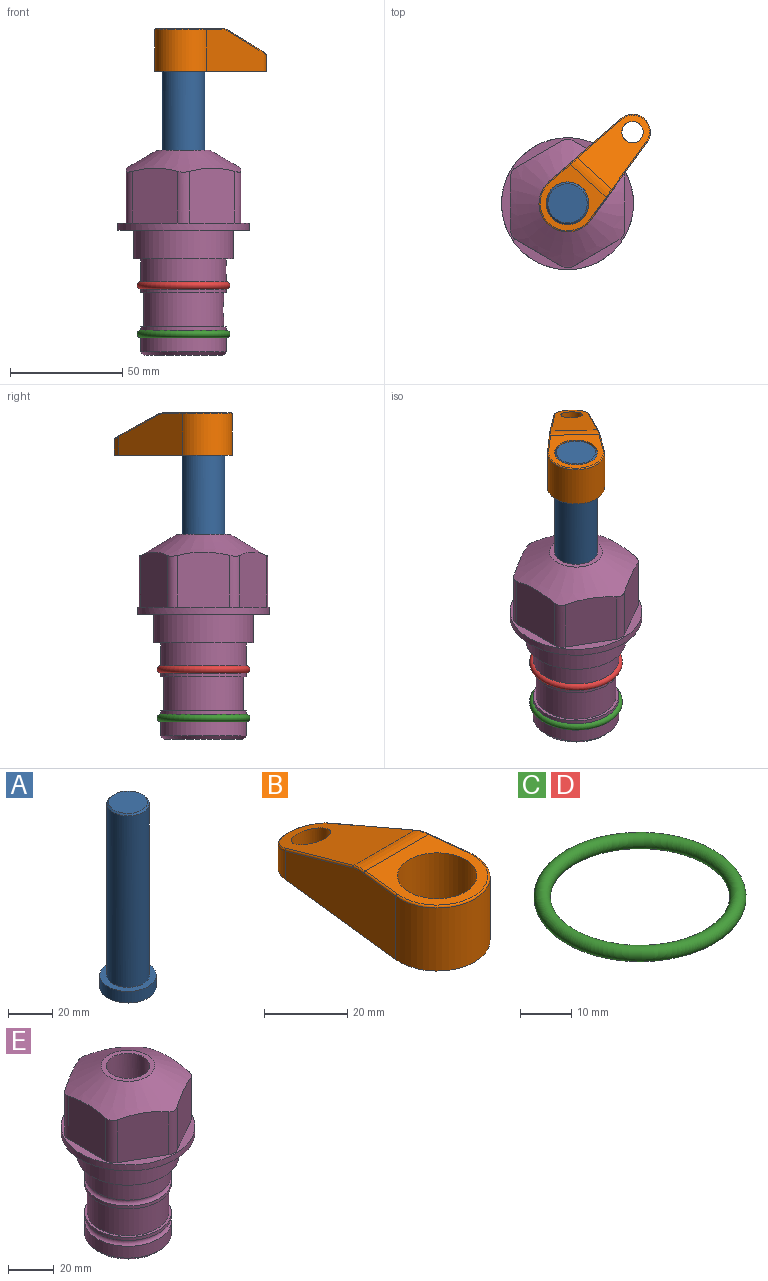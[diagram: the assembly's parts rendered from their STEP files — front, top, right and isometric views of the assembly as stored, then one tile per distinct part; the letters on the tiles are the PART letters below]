
ASSEMBLY  parts=5 mates=3
PART A: 6 faces, bbox 25.4x25.4x101.6 mm
  f0: plane 17.46x17.46mm, normal (0,0,1), area 239.5mm2, adj f5
  f1: plane 25.4x25.4mm, normal (0,0,-1), area 506.7mm2, adj f2
  f2: cylinder r=12.7mm len=25.4mm, axis (0,0,1), area 506.7mm2, adj f1,f3
  f3: plane 25.4x25.4mm, normal (0,0,1), area 221.7mm2, adj f2,f4
  f4: cylinder r=9.53mm len=94.46mm, axis (0,0,1), area 5653mm2, adj f3,f5
  f5: cone r=8.73mm half-angle=45deg, axis (0,0,-1), area 64.4mm2, adj f0,f4
PART B: 44 faces, bbox 27.5x64.5x19.1 mm
  f0: plane 2.3x0.95mm, normal (0,0,-1), area 1mm2, adj f25,f30,f34
  f1: plane 63.5x25.4mm, normal (0,0,-1), area 561.7mm2, adj f2,f3,f4,f5,f6,f7,f19,f20
  f2: cylinder r=12.7mm len=25.4mm, axis (0,0,-1), area 792.2mm2, adj f1,f3,f5,f13
  f3: plane 42.33x18.54mm, normal (0.99,0.11,0), area 647mm2, adj f1,f2,f4,f11,f12,f14
  f4: cylinder r=7.94mm len=15.78mm, axis (0,0,-1), area 158.6mm2, adj f1,f3,f5,f16
  f5: plane 42.33x18.54mm, normal (-0.99,0.11,0), area 647mm2, adj f1,f2,f4,f15,f17,f18
  f6: cylinder r=9.53mm len=19.05mm, axis (0,0,-1), area 1140.1mm2, adj f1,f8
  f7: cylinder r=4.76mm len=10.98mm, axis (0,0,-1), area 276.1mm2, adj f1,f9
  f8: plane 25.83x24.38mm, normal (0,0,1), area 262.2mm2, adj f6,f10,f11,f13,f15
  f9: plane 32.49x20.55mm, normal (0,0.34,0.94), area 489.9mm2, adj f7,f10,f14,f16,f18
  f10: cylinder r=12.7mm len=21.49mm, axis (-1,0,0), area 93.2mm2, adj f8,f9,f12,f17
  f11: cylinder r=0.51mm len=12.34mm, axis (0.11,-0.99,0), area 9.9mm2, adj f3,f8,f12,f13
  f12: bspline ~7.62x1.64mm, area 3.5mm2, adj f3,f10,f11,f14
  f13: torus R=12.19mm, axis (0,0,1), area 33.6mm2, adj f2,f8,f11,f15
  f14: cylinder r=0.51mm len=26.01mm, axis (0.1,-0.93,0.34), area 21.6mm2, adj f3,f9,f12,f16
  f15: cylinder r=0.51mm len=12.34mm, axis (0.11,0.99,0), area 9.9mm2, adj f5,f8,f13,f17
  f16: bspline ~15.78x7.05mm, area 15.7mm2, adj f4,f9,f14,f18
  f17: bspline ~7.62x1.64mm, area 3.5mm2, adj f5,f10,f15,f18
  f18: cylinder r=0.51mm len=26.01mm, axis (0.1,0.93,-0.34), area 21.6mm2, adj f5,f9,f16,f17
  f19: plane 21.6x14.29mm, normal (-0.99,-0.11,0), area 242.6mm2, adj f1,f26,f28,f34,f36,f38
  f20: plane 21.6x14.29mm, normal (0.99,-0.11,0), area 242.6mm2, adj f1,f27,f29,f37,f39,f41
  f21: cylinder r=12.7mm len=14.29mm, axis (0,0,-1), area 173.2mm2, adj f1,f26,f27,f30,f31,f33
  f22: cylinder r=7.94mm len=7.63mm, axis (0,0,-1), area 53.8mm2, adj f1,f28,f29,f42
  f23: plane 2.3x0.95mm, normal (0,0,-1), area 1mm2, adj f25,f33,f37
  f24: plane 17.94x12.32mm, normal (0,-0.34,-0.94), area 191.2mm2, adj f25,f38,f41,f42
  f25: cylinder r=9.53mm len=12.93mm, axis (-1,0,0), area 37.5mm2, adj f0,f23,f24,f31,f36,f39
  f26: cylinder r=1.59mm len=14.29mm, axis (0,0,-1), area 49mm2, adj f1,f19,f21,f32
  f27: cylinder r=1.59mm len=14.29mm, axis (0,0,-1), area 49mm2, adj f1,f20,f21,f35
  f28: cylinder r=1.59mm len=7.28mm, axis (0,0,-1), area 22.1mm2, adj f1,f19,f22,f40
  f29: cylinder r=1.59mm len=7.28mm, axis (0,0,-1), area 22.1mm2, adj f1,f20,f22,f43
  f30: torus R=14.29mm, axis (0,0,1), area 5.8mm2, adj f0,f21,f31,f32
  f31: bspline ~11.06x2.73mm, area 20.8mm2, adj f21,f25,f30,f33
  f32: sphere r=1.59mm, area 5.4mm2, adj f26,f30,f34
  f33: torus R=14.29mm, axis (0,0,1), area 5.8mm2, adj f21,f23,f31,f35
  f34: cylinder r=1.59mm len=1.68mm, axis (-0.11,0.99,0), area 2.4mm2, adj f0,f19,f32,f36
  f35: sphere r=1.59mm, area 5.4mm2, adj f27,f33,f37
  f36: bspline ~5.82x2.33mm, area 7.7mm2, adj f19,f25,f34,f38
  f37: cylinder r=1.59mm len=1.68mm, axis (0.11,0.99,0), area 2.4mm2, adj f20,f23,f35,f39
  f38: cylinder r=1.59mm len=18.33mm, axis (0.1,-0.93,0.34), area 46.7mm2, adj f19,f24,f36,f40
  f39: bspline ~5.82x2.33mm, area 7.7mm2, adj f20,f25,f37,f41
  f40: sphere r=1.59mm, area 3.6mm2, adj f28,f38,f42
  f41: cylinder r=1.59mm len=18.33mm, axis (0.1,0.93,-0.34), area 46.7mm2, adj f20,f24,f39,f43
  f42: bspline ~8.31x1.84mm, area 15.3mm2, adj f22,f24,f40,f43
  f43: sphere r=1.59mm, area 3.6mm2, adj f29,f41,f42
PART C: 1 faces, bbox 44.7x44.7x3.2 mm
  f0: torus R=19.05mm, axis (0,0,1), area 1193.9mm2
PART D: same geometry as C
PART E: 36 faces, bbox 58.7x58.7x91.2 mm
  f0: cylinder r=17.78mm len=35.56mm, axis (0,0,1), area 1670.8mm2, adj f23,f24,f31
  f1: cylinder r=19.05mm len=38.1mm, axis (0,0,1), area 1191.9mm2, adj f26,f27,f30
  f2: plane 58.66x58.66mm, normal (0,0,-1), area 1150.6mm2, adj f3,f28
  f3: cylinder r=29.33mm len=58.66mm, axis (0,0,-1), area 585.1mm2, adj f2,f4
  f4: plane 58.66x58.66mm, normal (0,0,1), area 475.9mm2, adj f3,f5,f6,f7,f8,f9,f10,f11
  f5: plane 24.5x20.32mm, normal (-0.5,0.87,0), area 562.8mm2, adj f4,f15,f16,f17
  f6: plane 24.5x20.32mm, normal (0.5,0.87,0), area 562.8mm2, adj f4,f14,f15,f17
  f7: plane 24.5x23.48mm, normal (1,0,0), area 562.8mm2, adj f4,f13,f14,f17
  f8: plane 24.5x20.32mm, normal (0.5,-0.87,0), area 562.8mm2, adj f4,f12,f13,f17
  f9: plane 24.5x20.32mm, normal (-0.5,-0.87,0), area 562.8mm2, adj f4,f11,f12,f17
  f10: plane 24.5x23.48mm, normal (-1,0,0), area 562.8mm2, adj f4,f11,f16,f17
  f11: cylinder r=5.08mm len=23.01mm, axis (0,0,-1), area 121.2mm2, adj f4,f9,f10,f17
  f12: cylinder r=5.08mm len=23.01mm, axis (0,0,-1), area 121.2mm2, adj f4,f8,f9,f17
  f13: cylinder r=5.08mm len=23.01mm, axis (0,0,-1), area 121.2mm2, adj f4,f7,f8,f17
  f14: cylinder r=5.08mm len=23.01mm, axis (0,0,-1), area 121.2mm2, adj f4,f6,f7,f17
  f15: cylinder r=5.08mm len=23.01mm, axis (0,0,-1), area 121.2mm2, adj f4,f5,f6,f17
  f16: cylinder r=5.08mm len=23.01mm, axis (0,0,-1), area 121.2mm2, adj f4,f5,f10,f17
  f17: cone r=11.73mm half-angle=60deg, axis (0,0,-1), area 2071.8mm2, adj f5,f6,f7,f8,f9,f10,f11,f12
  f18: plane 23.46x23.46mm, normal (0,0,1), area 147.4mm2, adj f17,f35
  f19: plane 34.93x34.93mm, normal (0,0,-1), area 958mm2, adj f29
  f20: cylinder r=19.05mm len=38.1mm, axis (0,0,1), area 760.1mm2, adj f21,f29
  f21: torus R=19.05mm, axis (0,0,1), area 565.3mm2, adj f20,f22
  f22: cylinder r=19.05mm len=38.1mm, axis (0,0,1), area 190mm2, adj f21,f23
  f23: plane 38.1x38.1mm, normal (0,0,1), area 146.9mm2, adj f0,f22
  f24: plane 38.1x38.1mm, normal (0,0,-1), area 146.9mm2, adj f0,f25
  f25: cylinder r=19.05mm len=38.1mm, axis (0,0,1), area 190mm2, adj f24,f26
  f26: torus R=19.05mm, axis (0,0,1), area 565.3mm2, adj f1,f25
  f27: plane 44.45x44.45mm, normal (0,0,-1), area 411.7mm2, adj f1,f28
  f28: cylinder r=22.23mm len=44.45mm, axis (0,0,1), area 1773.5mm2, adj f2,f27
  f29: cone r=19.05mm half-angle=45deg, axis (0,0,1), area 257.5mm2, adj f19,f20
  f30: cylinder r=3.17mm len=6.75mm, axis (-1,0,0), area 128mm2, adj f1,f33
  f31: cylinder r=3.17mm len=6.35mm, axis (-1,0,0), area 102.5mm2, adj f0,f33
  f32: plane 25.4x25.4mm, normal (0,0,1), area 506.7mm2, adj f33
  f33: cylinder r=12.7mm len=66.42mm, axis (0,0,-1), area 5236.2mm2, adj f30,f31,f32,f34
  f34: cone r=9.53mm half-angle=30deg, axis (0,0,-1), area 443.4mm2, adj f33,f35
  f35: cylinder r=9.53mm len=19.05mm, axis (0,0,-1), area 849mm2, adj f18,f34
PLACE A rot(axis=(0,0,1),47.6deg) t=(0,0,16.04)mm
PLACE B rot(axis=(0,0,-1),42.4deg) t=(0,0,70.65)mm
PLACE C t=(0,0,-21.59)mm
PLACE D at identity
PLACE E at identity fixed
MATE fastened C.f0 <-> E.f0  axis (0,0,1) through (0,0,-46.1)mm
MATE cylindrical A.f2 <-> E.f0  axis (0,0,1) through (0,0,41.67)mm
MATE fastened B.f2 <-> A.f2  axis (0,0,1) through (0,0,89.7)mm
